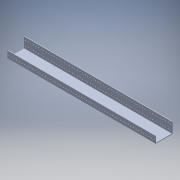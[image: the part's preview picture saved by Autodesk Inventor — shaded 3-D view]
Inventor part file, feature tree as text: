
AUTODESK INVENTOR PART (.ipt)
format: ipt  version: 2017 (Build 210142000, 142)  size: 342,016 bytes
history: native  units: in
note: dims shown in document units (in); Inventor stores cm internally (conversion verified against a paired STEP export)
features: other x5, reference x2, extrude x1, chamfer x1, sketch x1
ambient origin geometry x8: Origin, YZ Plane, XZ Plane, XY Plane, X Axis, Y Axis, Z Axis, Center Point
bodies: Solid1 (feature_tree)
feature tree (10):
  extrude  "Extrusion1"  Depth=2.0in
  chamfer  "Chamfer1"  Distance=0.125in Angle=45.0deg
  sketch  "Sketch1"  dims[d0=1.0in d1=0.0in d6=2.0in d7=0.125in d8=0.125in d9=45.0deg d10=29.0in]
  reference  "Reference1"
  reference  "Reference2"
  other  "LPattern4"
  other  "<userpath>\Documents\Inventor\2017 Robot\Robot Chassis.iam"
  other  "Robot Chassis.iam"
  other  "am-2951a_AM14U3_Outside_Plate:1"
  other  "am-2952a_AM14U3_Inside_Plate:1"
